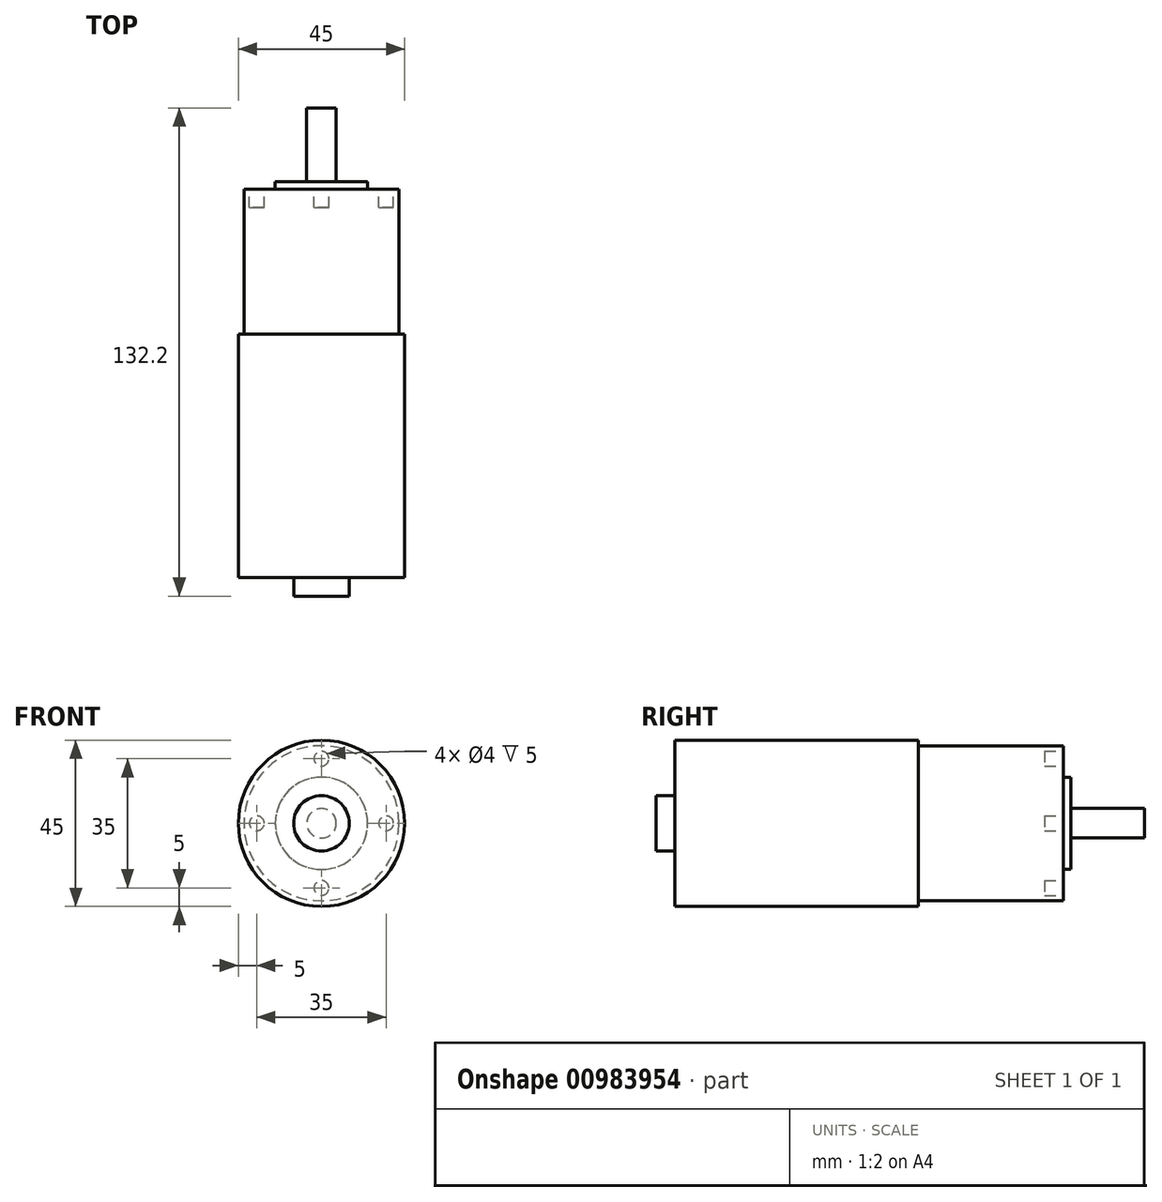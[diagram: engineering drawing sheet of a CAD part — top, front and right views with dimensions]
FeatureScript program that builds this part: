
annotation { "Feature Type Name" : "Feature", "Feature Type Description" : "" }
export const myFeature = defineFeature(function(context is Context, id is Id, definition is map)
    precondition{}
    {
        {
            var Q0;
            Q0=qCreatedBy(makeId("Front.planeOp"),FACE);
            var sketch = newSketch(context, id + "F0", { "sketchPlane" : qUnion([Q0])});
            skCircle(sketch, "E0", {"center": v(0, 0) * mm, "radius": 21 * mm});
            skSolve(sketch);
        }
        {
            var Q0;
            Q0=makeQuery(id+"F0.imprint","IMPRINT",FACE,{"disambiguationData":[TD([[makeQuery(id+"F0.imprint","IMPRINT",EDGE,{"derivedFrom":sQuery(id+"F0.wireOp",EDGE,"E0")}),1.0]])]});
            extrude(context, id + "F1", {"entities" : qUnion([Q0]), "depth" : 39.2 * mm, "offsetDistance" : 25 * mm});
        }
        {
            var Q0;
            Q0=makeQuery(id+"F1.opExtrude","CAP_FACE",FACE,{"disambiguationData":[OSD([sQuery(id+"F0.wireOp",EDGE,"E0")])],"isStart":false});
            var sketch = newSketch(context, id + "F2", { "sketchPlane" : qUnion([Q0])});
            skSolve(sketch);
        }
        {
            var Q0;
            Q0=makeQuery(id+"F1.opExtrude","CAP_FACE",FACE,{"disambiguationData":[OSD([sQuery(id+"F0.wireOp",EDGE,"E0")])],"isStart":true});
            var sketch = newSketch(context, id + "F3", { "sketchPlane" : qUnion([Q0])});
            skCircle(sketch, "E1", {"center": v(0, 0) * mm, "radius": 4 * mm});
            skSolve(sketch);
        }
        {
            var Q0;
            Q0 = qSketchRegion(id + "F3", true);
            extrude(context, id + "F4", {"entities" : qUnion([Q0]), "operationType" : NewBodyOperationType.ADD, "depth" : 22 * mm, "offsetDistance" : 25 * mm});
        }
        {
            var Q0;
            Q0=makeQuery(id+"F1.opExtrude","CAP_FACE",FACE,{"disambiguationData":[OSD([sQuery(id+"F0.wireOp",EDGE,"E0")])],"isStart":true});
            var sketch = newSketch(context, id + "F5", { "sketchPlane" : qUnion([Q0])});
            skCircle(sketch, "E2", {"center": v(0, 0) * mm, "radius": 12.5 * mm});
            skSolve(sketch);
        }
        {
            var Q0;
            Q0 = qSketchRegion(id + "F5", true);
            extrude(context, id + "F6", {"entities" : qUnion([Q0]), "operationType" : NewBodyOperationType.ADD, "depth" : 2 * mm, "offsetDistance" : 25 * mm});
        }
        {
            var Q0;
            Q0=makeQuery(id+"F2.imprint","IMPRINT",FACE,{"disambiguationData":[TD([[makeQuery(id+"F2.imprint","IMPRINT",EDGE,{"derivedFrom":makeQuery(id+"F1.opExtrude","CAP_EDGE",EDGE,{"disambiguationData":[OSD([sQuery(id+"F0.wireOp",EDGE,"E0")])],"isStart":false})}),1.0]])]});
            var sketch = newSketch(context, id + "F7", { "sketchPlane" : qUnion([Q0])});
            skCircle(sketch, "E3", {"center": v(0, 0) * mm, "radius": 22.5 * mm});
            skSolve(sketch);
        }
        {
            var Q0;
            Q0 = qSketchRegion(id + "F7", true);
            extrude(context, id + "F8", {"entities" : qUnion([Q0]), "operationType" : NewBodyOperationType.ADD, "depth" : 66 * mm, "offsetDistance" : 25 * mm});
        }
        {
            var Q0;
            Q0=makeQuery(id+"F8.opExtrude","CAP_FACE",FACE,{"disambiguationData":[OSD([sQuery(id+"F7.wireOp",EDGE,"E3")])],"isStart":false});
            var sketch = newSketch(context, id + "F9", { "sketchPlane" : qUnion([Q0])});
            skCircle(sketch, "E4", {"center": v(0, 0) * mm, "radius": 7.5 * mm});
            skSolve(sketch);
        }
        {
            var Q0;
            Q0 = qSketchRegion(id + "F9", true);
            extrude(context, id + "F10", {"entities" : qUnion([Q0]), "operationType" : NewBodyOperationType.ADD, "depth" : 5 * mm, "offsetDistance" : 25 * mm});
        }
        {
            var Q0;
            Q0=makeQuery(id+"F1.opExtrude","CAP_FACE",FACE,{"disambiguationData":[OSD([sQuery(id+"F0.wireOp",EDGE,"E0")])],"isStart":true});
            var sketch = newSketch(context, id + "F11", { "sketchPlane" : qUnion([Q0])});
            skCircle(sketch, "E5", {"center": v(0, 17.5) * mm, "radius": 2 * mm});
            skCircle(sketch, "E6", {"center": v(17.5, 0) * mm, "radius": 2 * mm});
            skCircle(sketch, "E7", {"center": v(0, -17.5) * mm, "radius": 2 * mm});
            skCircle(sketch, "E8", {"center": v(-17.5, 0) * mm, "radius": 2 * mm});
            skSolve(sketch);
        }
        {
            var Q0;
            Q0=makeQuery(id+"F11.imprint","IMPRINT",FACE,{"disambiguationData":[TD([[makeQuery(id+"F11.imprint","IMPRINT",EDGE,{"derivedFrom":sQuery(id+"F11.wireOp",EDGE,"E8")}),1.0]])]});
            var Q1;
            Q1=makeQuery(id+"F11.imprint","IMPRINT",FACE,{"disambiguationData":[TD([[makeQuery(id+"F11.imprint","IMPRINT",EDGE,{"derivedFrom":sQuery(id+"F11.wireOp",EDGE,"E5")}),1.0]])]});
            var Q2;
            Q2=makeQuery(id+"F11.imprint","IMPRINT",FACE,{"disambiguationData":[TD([[makeQuery(id+"F11.imprint","IMPRINT",EDGE,{"derivedFrom":sQuery(id+"F11.wireOp",EDGE,"E6")}),1.0]])]});
            var Q3;
            Q3=makeQuery(id+"F11.imprint","IMPRINT",FACE,{"disambiguationData":[TD([[makeQuery(id+"F11.imprint","IMPRINT",EDGE,{"derivedFrom":sQuery(id+"F11.wireOp",EDGE,"E7")}),1.0]])]});
            extrude(context, id + "F12", {"entities" : qUnion([Q0, Q1, Q2, Q3]), "operationType" : NewBodyOperationType.REMOVE, "oppositeDirection" : true, "depth" : 5 * mm, "offsetDistance" : 25 * mm});
        }
    });
